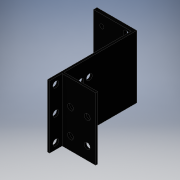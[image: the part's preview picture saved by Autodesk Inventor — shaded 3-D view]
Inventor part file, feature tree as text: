
AUTODESK INVENTOR PART (.ipt)
format: ipt  version: 2016 (Build 200138000, 138)  size: 187,904 bytes
history: native  units: mm
features: sketch x8, hole x5, extrude x3
ambient origin geometry x8: Origin, YZ Plane, XZ Plane, XY Plane, X Axis, Y Axis, Z Axis, Center Point
bodies: Body1 (feature_tree)
feature tree (16):
  extrude  "Extrusion2"  Depth=45.0mm
  extrude  "Extrusion3"  Depth=1.5mm
  hole  "Hole2"  [1 undecoded]
  hole  "Hole3"  [1 undecoded]
  hole  "Hole4"  [1 undecoded]
  extrude  "Extrusion4"  Depth=4.6mm
  hole  "Hole6"  [1 undecoded]
  hole  "Hole7"  [1 undecoded]
  sketch  "Sketch3"  dims[d27=27.0mm d28=45.0mm]
  sketch  "Sketch4"  dims[d29=2.5mm d30=0.0mm d31=1.5mm]
  sketch  "Sketch5"  dims[d32=45.0mm d33=60.0mm d34=2.5mm d35=0.0mm d36=0.0mm]
  sketch  "Sketch6"  dims[d45=4.6mm d46=3.5mm]
  sketch  "Sketch7"  dims[d47=3.5mm d50=4.6mm]
  sketch  "Sketch8"  dims[d51=3.5mm d52=4.6mm]
  sketch  "Sketch10"  dims[d53=4.6mm d54=6.0mm d55=4.0mm d56=2.0mm d57=90.0deg d58=8.0mm d59=0.0mm d61=3.5mm]
  sketch  "Sketch11"  dims[d62=3.5mm d63=3.5mm d64=3.0mm d65=6.0mm d66=7.5mm d67=3.0mm d68=18.0mm d69=3.0mm d70=6.0mm d71=4.0mm d72=2.0mm d73=90.0deg d74=8.0mm d75=0.0mm d76=4.3mm d77=4.5mm d78=4.5mm d79=4.3mm d80=4.5mm d81=4.5mm d82=4.3mm d83=4.3mm d84=6.0mm d85=4.0mm d86=2.0mm d87=90.0deg d88=8.0mm d89=0.0mm d90=45.0mm d91=1.5mm d92=52.0mm d93=24.0mm d94=0.0mm d95=4.25mm d96=9.0mm d97=6.0mm d100=4.25mm d102=9.0mm d110=4.25mm d111=6.0mm d112=4.0mm d113=2.0mm d114=90.0deg d115=8.0mm d116=20.594885mm d117=4.25mm d119=12.0mm d120=6.0mm d121=4.25mm d122=6.0mm d123=4.25mm d124=6.0mm d125=4.25mm d126=6.0mm d127=4.0mm d128=2.0mm d129=90.0deg d130=8.0mm d131=20.594885mm]
note: 5 required parameter values undecoded (feature->parameter linkage not recoverable at this tier; creation-order binding heuristic only, values carry confidence <= 0.55)
